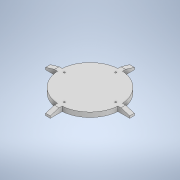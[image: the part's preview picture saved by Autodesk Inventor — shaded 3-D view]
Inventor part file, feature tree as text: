
AUTODESK INVENTOR PART (.ipt)
format: ipt  version: 2021 (Build 250183000, 183)  size: 196,608 bytes
history: native  units: mm
features: extrude x4, chamfer x4, sketch x4, plane x1
ambient origin geometry x8: Origin, YZ Plane, XZ Plane, XY Plane, X Axis, Y Axis, Z Axis, Center Point
bodies: Solid1 (feature_tree)
feature tree (13):
  plane  "Work Plane17"
  extrude  "Extrusion62"  Depth=10.0mm TaperAngle=0.0deg
  extrude  "Extrusion63"  Depth=10.0mm
  chamfer  "Chamfer1"  Distance=10.0mm
  chamfer  "Chamfer2"  Distance=50.0mm
  chamfer  "Chamfer3"  Distance=50.0mm
  chamfer  "Chamfer4"  Distance=10.0mm
  extrude  "Extrusion64"  Depth=10.0mm TaperAngle=0.0deg
  extrude  "Extrusion65"  Depth=3.5mm TaperAngle=45.0deg
  sketch  "Sketch131"  dims[d245=130.0mm d246=10.0mm d247=0.0mm]
  sketch  "Sketch132"  dims[d248=10.0mm d249=50.0mm]
  sketch  "Sketch135"  dims[d250=50.0mm]
  sketch  "Sketch136"  dims[d251=10.0mm d252=10.0mm d253=50.0mm d254=50.0mm d255=10.0mm d256=10.0mm d257=0.0mm d258=18.75mm d259=5.5mm d260=45.0deg d261=18.75mm d262=5.5mm d263=45.0deg d264=18.75mm d265=5.5mm d266=45.0deg d267=18.75mm d268=5.5mm d269=45.0deg d279=110.108mm d280=3.1mm d281=3.1mm d282=3.1mm d283=3.1mm d284=30.0mm d285=0.0mm d286=8.0mm d287=8.0mm d288=8.0mm d289=8.0mm d290=3.5mm d291=0.0mm d9=0.5mm d10=0.872665mm d11=0.5mm d12=0.872665mm d13=0.5mm d14=0.872665mm d15=0.5mm d16=0.872665mm d17=0.872665mm d18=0.5mm d19=0.872665mm d29=0.5mm d30=0.872665mm d31=0.5mm d32=0.872665mm d53=0.5mm d54=0.872665mm d55=0.5mm d56=0.872665mm d59=0.5mm d60=0.872665mm d61=0.5mm d62=0.872665mm d69=0.5mm d70=0.872665mm d71=0.5mm d72=0.872665mm d116=0.5mm d117=0.872665mm d118=0.5mm d119=0.872665mm d125=0.5mm d126=0.872665mm d127=0.5mm d128=0.872665mm d129=0.872665mm d130=0.5mm d131=0.872665mm d135=0.5mm d136=0.872665mm d137=0.5mm d138=0.872665mm d139=0.5mm d140=0.872665mm d141=0.5mm d142=0.872665mm d173=0.5mm d174=0.872665mm d175=0.5mm d176=0.872665mm d177=0.5mm d178=0.872665mm d179=0.5mm d180=0.872665mm d182=0.5mm d183=0.872665mm d184=0.5mm d185=0.872665mm d197=0.5mm d198=0.872665mm d199=0.5mm d200=0.872665mm d228=0.5mm d229=0.872665mm d230=0.5mm d231=0.872665mm d238=0.5mm d239=0.872665mm d240=0.5mm d241=0.872665mm]
